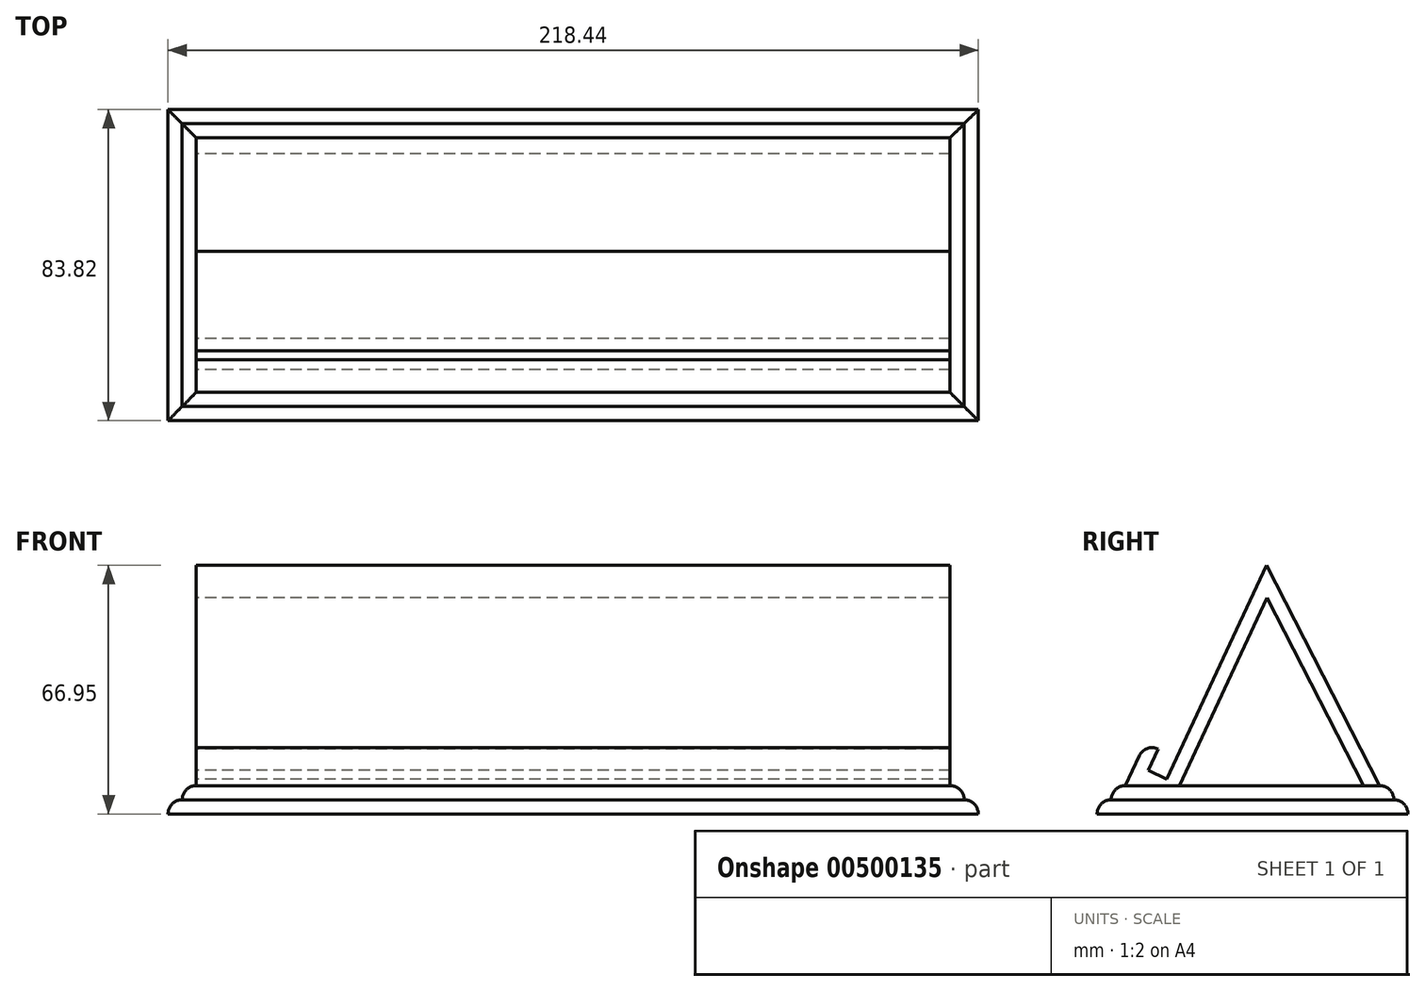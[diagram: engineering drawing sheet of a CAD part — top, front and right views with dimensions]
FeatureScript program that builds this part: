
annotation { "Feature Type Name" : "Feature", "Feature Type Description" : "" }
export const myFeature = defineFeature(function(context is Context, id is Id, definition is map)
    precondition{}
    {
        {
            var Q0;
            Q0=qCreatedBy(makeId("Right.planeOp"),FACE);
            var sketch = newSketch(context, id + "F0", { "sketchPlane" : qUnion([Q0])});
            skLineSegment(sketch, "E0.bottom", {"start": v(-38.1, -1.9) * mm, "end": v(38.1, -1.9) * mm});
            skLineSegment(sketch, "E0.top", {"start": v(-38.1, 1.9) * mm, "end": v(38.1, 1.9) * mm});
            skLineSegment(sketch, "E0.left", {"start": v(-38.1, -1.9) * mm, "end": v(-38.1, 1.9) * mm});
            skLineSegment(sketch, "E0.right", {"start": v(38.1, -1.9) * mm, "end": v(38.1, 1.9) * mm});
            skPoint(sketch, "E0.middle", {"position": v(0, 0) * mm});
            skLineSegment(sketch, "E1", {"start": v(34.3, 1.9) * mm, "end": v(3.75, 61.24) * mm});
            skLineSegment(sketch, "E2", {"start": v(3.75, 61.24) * mm, "end": v(-23.09, 3.69) * mm});
            skLineSegment(sketch, "E3", {"start": v(-23.09, 3.69) * mm, "end": v(-28.15, 6.05) * mm});
            skLineSegment(sketch, "E4", {"start": v(-28.15, 6.05) * mm, "end": v(-25.47, 11.8) * mm});
            skLineSegment(sketch, "E5", {"start": v(-25.47, 11.8) * mm, "end": v(-28.92, 13.42) * mm});
            skLineSegment(sketch, "E6", {"start": v(-28.92, 13.42) * mm, "end": v(-34.3, 1.9) * mm});
            skLineSegment(sketch, "E7.bottom", {"start": v(-41.91, -5.72) * mm, "end": v(41.91, -5.72) * mm});
            skLineSegment(sketch, "E7.top", {"start": v(-41.91, -1.9) * mm, "end": v(41.91, -1.9) * mm});
            skLineSegment(sketch, "E7.left", {"start": v(-41.91, -5.72) * mm, "end": v(-41.91, -1.9) * mm});
            skLineSegment(sketch, "E7.right", {"start": v(41.91, -5.72) * mm, "end": v(41.91, -1.9) * mm});
            skPoint(sketch, "E7.middle", {"position": v(0, -3.81) * mm});
            skPoint(sketch, "E7.middle.positionSnap0", {"position": v(0, -1.9) * mm});
            skPoint(sketch, "E7.centerSnap0", {"position": v(0, -1.9) * mm});
            skLineSegment(sketch, "E8.0", {"start": v(3.92, 52.59) * mm, "end": v(-19.72, 1.9) * mm});
            skLineSegment(sketch, "E8.1", {"start": v(30, 1.9) * mm, "end": v(3.92, 52.59) * mm});
            skSolve(sketch);
        }
        {
            var Q0;
            {var subQ0=sQuery(id+"F0.wireOp",EDGE,"E1");Q0=makeQuery(id+"F0.imprint","IMPRINT",FACE,{"disambiguationData":[TD([[makeQuery(id+"F0.imprint","IMPRINT",EDGE,{"derivedFrom":subQ0}),1.0]])]});}
            extrude(context, id + "F1", {"entities" : qUnion([Q0]), "endBound" : BoundingType.SYMMETRIC, "depth" : 203.2 * mm, "offsetDistance" : 25.4 * mm});
        }
        {
            var Q0;
            Q0=makeQuery(id+"F0.imprint","IMPRINT",FACE,{"disambiguationData":[TD([[makeQuery(id+"F0.imprint","IMPRINT",EDGE,{"derivedFrom":sQuery(id+"F0.wireOp",EDGE,"E0.bottom")}),1.0]])]});
            extrude(context, id + "F2", {"entities" : qUnion([Q0]), "operationType" : NewBodyOperationType.ADD, "endBound" : BoundingType.SYMMETRIC, "depth" : 210.82 * mm, "offsetDistance" : 25.4 * mm});
        }
        {
            var Q0;
            Q0=makeQuery(id+"F2.opExtrude","CAP_EDGE",EDGE,{"disambiguationData":[OSD([sQuery(id+"F0.wireOp",EDGE,"E0.top")])],"isStart":true});
            var Q1;
            Q1=makeQuery(id+"F2.opExtrude","SWEPT_EDGE",EDGE,{"disambiguationData":[OSD([sQuery(id+"F0.wireOp",EDGE,"E0.top"),sQuery(id+"F0.wireOp",EDGE,"E0.left")])]});
            var Q2;
            Q2=makeQuery(id+"F2.opExtrude","SWEPT_EDGE",EDGE,{"disambiguationData":[OSD([sQuery(id+"F0.wireOp",EDGE,"E0.top"),sQuery(id+"F0.wireOp",EDGE,"E0.right")])]});
            var Q3;
            Q3=makeQuery(id+"F2.opExtrude","CAP_EDGE",EDGE,{"disambiguationData":[OSD([sQuery(id+"F0.wireOp",EDGE,"E0.top")])],"isStart":false});
            fillet(context, id + "F3", {"entities" : qUnion([Q0, Q1, Q2, Q3]), "tangentPropagation" : true, "radius" : 3.8 * mm, "defaultsChanged" : true, "vertexSettings" : [], "allowEdgeOverflow" : false});
        }
        {
            var Q0;
            Q0=makeQuery(id+"F1.opExtrude","SWEPT_EDGE",EDGE,{"disambiguationData":[OSD([sQuery(id+"F0.wireOp",EDGE,"E5"),sQuery(id+"F0.wireOp",EDGE,"E6")])]});
            fillet(context, id + "F4", {"entities" : qUnion([Q0]), "tangentPropagation" : true, "radius" : 3.8 * mm, "defaultsChanged" : true, "vertexSettings" : [], "allowEdgeOverflow" : false});
        }
        {
            var Q0;
            {var subQ1=sQuery(id+"F0.wireOp",EDGE,"E0.bottom");Q0=makeQuery(id+"F0.imprint","IMPRINT",FACE,{"disambiguationData":[TD([[makeQuery(id+"F0.imprint","IMPRINT",EDGE,{"derivedFrom":subQ1}),-1.0]])]});}
            extrude(context, id + "F5", {"entities" : qUnion([Q0]), "operationType" : NewBodyOperationType.ADD, "endBound" : BoundingType.SYMMETRIC, "depth" : 218.44 * mm, "offsetDistance" : 25.4 * mm});
        }
        {
            var Q0;
            Q0=makeQuery(id+"F5.opExtrude","CAP_EDGE",EDGE,{"disambiguationData":[OSD([sQuery(id+"F0.wireOp",EDGE,"E0.bottom"),sQuery(id+"F0.wireOp",EDGE,"E7.top")])],"isStart":true});
            var Q1;
            Q1=makeQuery(id+"F5.opExtrude","SWEPT_EDGE",EDGE,{"disambiguationData":[OSD([sQuery(id+"F0.wireOp",EDGE,"E7.top"),sQuery(id+"F0.wireOp",EDGE,"E7.right")])]});
            var Q2;
            Q2=makeQuery(id+"F5.opExtrude","CAP_EDGE",EDGE,{"disambiguationData":[OSD([sQuery(id+"F0.wireOp",EDGE,"E0.bottom"),sQuery(id+"F0.wireOp",EDGE,"E7.top")])],"isStart":false});
            var Q3;
            Q3=makeQuery(id+"F5.opExtrude","SWEPT_EDGE",EDGE,{"disambiguationData":[OSD([sQuery(id+"F0.wireOp",EDGE,"E7.top"),sQuery(id+"F0.wireOp",EDGE,"E7.left")])]});
            fillet(context, id + "F6", {"entities" : qUnion([Q0, Q1, Q2, Q3]), "tangentPropagation" : true, "radius" : 3.8 * mm, "defaultsChanged" : false, "vertexSettings" : [], "allowEdgeOverflow" : false});
        }
    });
